# Revit family: IS_CeraPlus_A6144_BIM_BE
name_source: partatom
category: Plumbing Fixtures
revit_build: Autodesk Revit 2015 (Build: 20140606_1530(x64)
units: mm (PartAtom-declared; Revit-internal decimal feet)

## types (1)
- A6144AA - CeraPlus Robinet lavabo électronique sans mélange (branchement sur le secteur 230 V)
    Accesoires = www.idealstandard.be
    Afwerking = Chroom
    Auteur = Ideal Standard Produktions-GmbH
    Barcode = 4015413332606
    Bedieningkraan = magnetische klep
    Bedieningkraanwerk = electronisch
    Beschrijvinggarantie = Fabrieksgarantie
    BimObjectNaam = ISI_IdealStandard_Robinet_CeraPlus_A6144AA
    Breedte = 0
    BrutoGewicht = 0
    Cost = 0 $
    Debiet = 4.7L/min | 3bar
    Default Elevation = 1219 mm
    Description = CeraPlus Robinet lavabo électronique sans mélange (branchement sur le secteur 230 V)
    Diepte = 0 mm  [stored 0 ft]
    Dimensions = 163 x 60 x 138 mm
    DuurEenheid = jaar
    Eigenschappen = CeraPlus elektronische wastafelmengkraan DN15 zonder menging. Vaste uitloop anti-diefstal laminaire perlator. Geïntegreerde electronica. Netaansluiting (230V) Veiligheidsstop naa 55 sec. zonder waste. Sprong 112mm. Hoogte uitloop 136mm. Flexibele aansluitleidingen. Onderbevestiging (met aansluiting G1/2). Geluidsniveau volgens norm DIN 4109, Groep 1.
    Garantieonderdelen = 5
    Hauteur = 138 mm  [stored 0.452756 ft]
    IfcExportAs = IfcValveTypes
    IfcExportType = TAPS
    Installatieinstructies = www.idealstandard.be
    Kleur = Chroom
    Largeur = 60 mm
    Lengte = 0 mm  [stored 0 ft]
    Longueur = 163 mm
    Manufacturer = www.idealstandard.be
    Materiaal = messing verchroomd
    Merk = Ideal Standard
    Model = A6144AA
    Nettogewicht = 1.6
    Normen = DIN 4109
    Productinformatie = www.idealstandard.be
    Telefoonnummer = 0032 2 325 66 00
    Testdruk = 10 bar
    Typeconnectie = Sanitair
    Typekraanwerk = wastafel
    URL = www.idealstandard.be
    Uniclass2015Beschrijving = Wash basin taps
    Uniclass2015Referentie = Pr_40_20_87_98
    Uniclass2015Version = Products v1.1
    Urlproducent = www.idealstandard.be
    Versie = 1
    Vervangingskosten = 0
    Verwachtelevensduur = 25 jaar
    Volumeunits = liter
    Werkdruk = 1-5 bar

note: [stored X ft] marks values corroborated as IEEE doubles in the binary element streams (Revit-internal decimal feet)

## geometry (parser evidence)
native form markers: Blend x2, Sweep x3
no freeform markers — native parametric forms only
